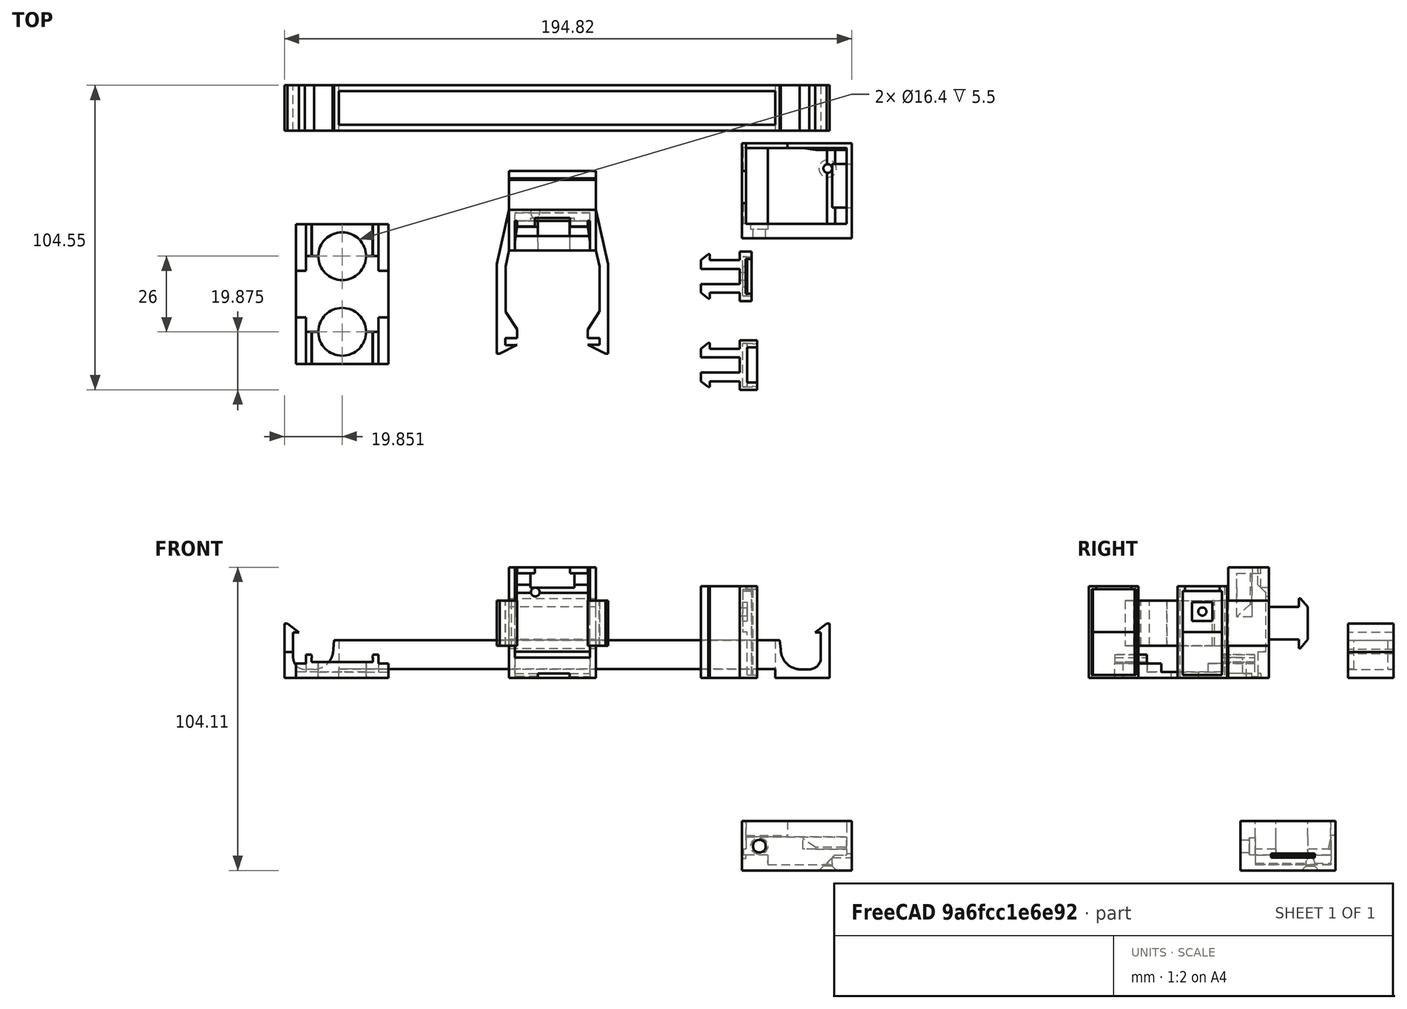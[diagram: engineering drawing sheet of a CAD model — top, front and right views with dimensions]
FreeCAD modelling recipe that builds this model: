
FCSTD DOCUMENT  (FreeCAD 0.18.4R)
Label: hanger.station.V2
License: All rights reserved
LicenseURL: http://en.wikipedia.org/wiki/All_rights_reserved
objects: Part::Feature×16, Part::Extrusion×12, Part::Cut×8, Part::Part2DObjectPython×4, Part::MultiFuse×3
note: 43 computed .brp shape members not serialized (recipe doc carries the construction recipe); baked Part::Feature solids carry a one-line shape summary decoded from their .brp

FEATURE [Part::Feature] Face009
  shape: bbox 55.84 x 2 x 0.0003342 mm, 1 faces, 0 solids (baked)
FEATURE [Part::Feature] Cut004001  label="Cut005"
  shape: bbox 187.2 x 15.6 x 18.67 mm, 45 faces, 2 solids (baked)
FEATURE [Part::Extrusion] Extrusion008
  Base = -> Face009
  Dir = (2.8e-15,1.09e-14,1)
  DirMode = 0
  FaceMakerClass = Part::FaceMakerBullseye
  LengthFwd = 0
  LengthRev = 0
  Solid = true
  Symmetric = false
FEATURE [Part::Cut] Cut004002
  Base = -> Cut004001
  Tool = -> Extrusion008
FEATURE [Part::Feature] Face010
  shape: bbox 94.1 x 2 x 0.0003342 mm, 1 faces, 0 solids (baked)
FEATURE [Part::Extrusion] Extrusion009
  Base = -> Face010
  Dir = (4.6e-15,4.225e-13,1)
  DirMode = 0
  FaceMakerClass = Part::FaceMakerBullseye
  LengthFwd = 0
  LengthRev = 0
  Solid = true
  Symmetric = false
FEATURE [Part::Cut] Cut004003
  Base = -> Cut004002
  Tool = -> Extrusion009
FEATURE [Part::Feature] Face011
  shape: bbox 149.9 x 2 x 0.0003342 mm, 1 faces, 0 solids (baked)
FEATURE [Part::Extrusion] Extrusion010
  Base = -> Face011
  Dir = (3.5e-15,3.507e-13,1)
  DirMode = 0
  FaceMakerClass = Part::FaceMakerBullseye
  LengthFwd = 0
  LengthRev = 0
  Solid = true
  Symmetric = false
FEATURE [Part::Cut] Cut004004
  Base = -> Cut004003
  Tool = -> Extrusion010
FEATURE [Part::Feature] Fusion009012003002002002002004002005016019  label="Fusion009012003002002002002004002005016018"
  Placement = pos=(-73.7708,-311.433,-201.044) rot=(1,0,0;3.14159rad)
  shape: bbox 31.67 x 48 x 8 mm, 52 faces (baked)
FEATURE [Part::Feature] Fusion009012003002002002002004002005016028006003003001  label="Fusion009012003002002002002004002005016028006003004"
  shape: bbox 38.26 x 62.71 x 38 mm, 95 faces (baked)
FEATURE [Part::Feature] Face033
  Placement = pos=(-33.3461,-156.309,-125.386) rot=(0,0,1;0rad)
  shape: bbox 12 x 2.022e-05 x 2 mm, 1 faces, 0 solids (baked)
FEATURE [Part::Extrusion] Extrusion048
  Base = -> Face033
  Dir = (9.45573e-10,1,-2.9767e-11)
  DirMode = 0
  FaceMakerClass = Part::FaceMakerBullseye
  LengthFwd = 0
  LengthRev = 0
  Solid = true
  Symmetric = false
FEATURE [Part::Cut] Cut
  Base = -> Fusion009012003002002002002004002005016028006003003001
  Tool = -> Extrusion048
FEATURE [Part::Feature] Fusion009012003002002002002004002005016028006003003003001  label="Fusion009012003002002002002004002005016028006003003004"
  shape: bbox 19.3 x 17 x 31.54 mm, 34 faces (baked)
FEATURE [Part::Feature] Fusion  label="Fusion009012003002002002002004002005016028006003003005"
  Placement = pos=(0,-30.409,4.3e-14) rot=(0,0,1;0rad)
  shape: bbox 19.3 x 17 x 31.54 mm, 34 faces (baked)
FEATURE [Part::Feature] Face
  shape: bbox 3e-07 x 17 x 31.54 mm, 1 faces, 0 solids (baked)
FEATURE [Part::Extrusion] Extrusion
  Base = -> Face
  Dir = (-1.9,0,1.33e-14)
  DirMode = 0
  FaceMakerClass = Part::FaceMakerBullseye
  LengthFwd = 0
  LengthRev = 0
  Solid = true
  Symmetric = false
FEATURE [Part::Cut] Cut004005
  Base = -> Fusion009012003002002002002004002005016028006003003003001
  Tool = -> Extrusion
FEATURE [Part::Part2DObjectPython] Rectangle  # Draft 2D object (typed FeaturePython)
  ChamferSize = 0
  Columns = 1
  FilletRadius = 0
  Height = 46.0733
  Length = 21.7717
  MakeFace = true
  Placement = pos=(142.488,-191.81,-130.532) rot=(0.57735,0.57735,0.57735;2.0944rad)
  Rows = 1
  Support = -> [Cut004005]
FEATURE [Part::Extrusion] Extrusion049
  Base = -> Rectangle
  Dir = (25.9534,0,0)
  DirMode = 0
  FaceMakerClass = Part::FaceMakerBullseye
  LengthFwd = 0
  LengthRev = 0
  Solid = true
  Symmetric = false
FEATURE [Part::Cut] Cut004006
  Base = -> Cut004005
  Tool = -> Extrusion049
FEATURE [Part::Feature] Face034
  shape: bbox 3.1 x 3e-07 x 29.54 mm, 1 faces, 0 solids (baked)
FEATURE [Part::Extrusion] Extrusion050
  Base = -> Face034
  Dir = (2.4e-15,0.79997,-4e-16)
  DirMode = 0
  FaceMakerClass = Part::FaceMakerBullseye
  LengthFwd = 0
  LengthRev = 0
  Solid = true
  Symmetric = false
FEATURE [Part::Feature] Face035
  shape: bbox 3.1 x 3e-07 x 29.54 mm, 1 faces, 0 solids (baked)
FEATURE [Part::Extrusion] Extrusion051
  Base = -> Face035
  Dir = (1.8e-15,-0.79997,4e-16)
  DirMode = 0
  FaceMakerClass = Part::FaceMakerBullseye
  LengthFwd = 0
  LengthRev = 0
  Solid = true
  Symmetric = false
FEATURE [Part::MultiFuse] Fusion009012003002002002002004002005016028006003003003002
  Shapes = -> [Extrusion051,Extrusion050,Cut004006]
FEATURE [Part::Feature] Face036
  shape: bbox 3.1 x 13.4 x 3e-07 mm, 1 faces, 0 solids (baked)
FEATURE [Part::Extrusion] Extrusion052
  Base = -> Face036
  Dir = (-7e-15,-4e-16,-0.74275)
  DirMode = 0
  FaceMakerClass = Part::FaceMakerBullseye
  LengthFwd = 0
  LengthRev = 0
  Solid = true
  Symmetric = false
FEATURE [Part::MultiFuse] Fusion009012003002002002002004002005016028006003003003003
  Shapes = -> [Extrusion052,Fusion009012003002002002002004002005016028006003003003002]
FEATURE [Part::Feature] Fusion009012003002002002002004002005016028006003003003003001  label="Fusion009012003002002002002004002005016028006003003003004"
  shape: bbox 17.4 x 17 x 31.54 mm, 30 faces (baked)
FEATURE [Part::Feature] Face037
  shape: bbox 5e-07 x 12 x 1.741 mm, 1 faces, 0 solids (baked)
FEATURE [Part::Extrusion] Extrusion053
  Base = -> Face037
  Dir = (-0.5,0,0)
  DirMode = 0
  FaceMakerClass = Part::FaceMakerBullseye
  LengthFwd = 0
  LengthRev = 0
  Solid = true
  Symmetric = false
FEATURE [Part::Cut] Cut004007
  Base = -> Fusion009012003002002002002004002005016028006003003003003001
  Tool = -> Extrusion053
FEATURE [Part::Part2DObjectPython] Rectangle001  # Draft 2D object (typed FeaturePython)
  ChamferSize = 0
  Columns = 1
  FilletRadius = 0
  Height = 6.5
  Length = 7
  MakeFace = true
  Placement = pos=(139.388,-178.123,-99.352) rot=(0.57735,-0.57735,0.57735;4.18879rad)
  Rows = 1
FEATURE [Part::Extrusion] Extrusion055
  Base = -> Rectangle001
  Dir = (1.5,4.3e-15,-7.5e-15)
  DirMode = 0
  FaceMakerClass = Part::FaceMakerBullseye
  LengthFwd = 0
  LengthRev = 0
  Solid = true
  Symmetric = false
FEATURE [Part::Part2DObjectPython] Circle001  # Draft 2D object (typed FeaturePython)
  FirstAngle = 0
  LastAngle = 0
  MakeFace = true
  Placement = pos=(140.888,-181.623,-102.602) rot=(0.57735,-0.57735,0.57735;4.18879rad)
  Radius = 1.4
  Support = -> [Extrusion055]
FEATURE [Part::Extrusion] Extrusion056
  Base = -> Circle001
  Dir = (-9.15,-7.1e-15,5.08e-14)
  DirMode = 0
  FaceMakerClass = Part::FaceMakerBullseye
  LengthFwd = 0
  LengthRev = 0
  Solid = true
  Symmetric = false
FEATURE [Part::MultiFuse] Fusion009012003002002002002004002005016028006003003003003002
  Shapes = -> [Cut004007,Extrusion055]
FEATURE [Part::Cut] Cut004008
  Base = -> Fusion009012003002002002002004002005016028006003003003003002
  Tool = -> Extrusion056
FEATURE [Part::Part2DObjectPython] Rectangle002  # Draft 2D object (typed FeaturePython)
  ChamferSize = 0
  Columns = 1
  FilletRadius = 0
  Height = 4.95987
  Length = 11
  MakeFace = true
  Placement = pos=(69.0449,-167.793,-123.886) rot=(1,0,0;3.14159rad)
  Rows = 1
  Support = -> [Cut]
FEATURE [Part::Feature] Fusion001001  label="Fusion002"
  shape: bbox 37.73 x 32.6 x 17 mm, 55 faces (baked)
